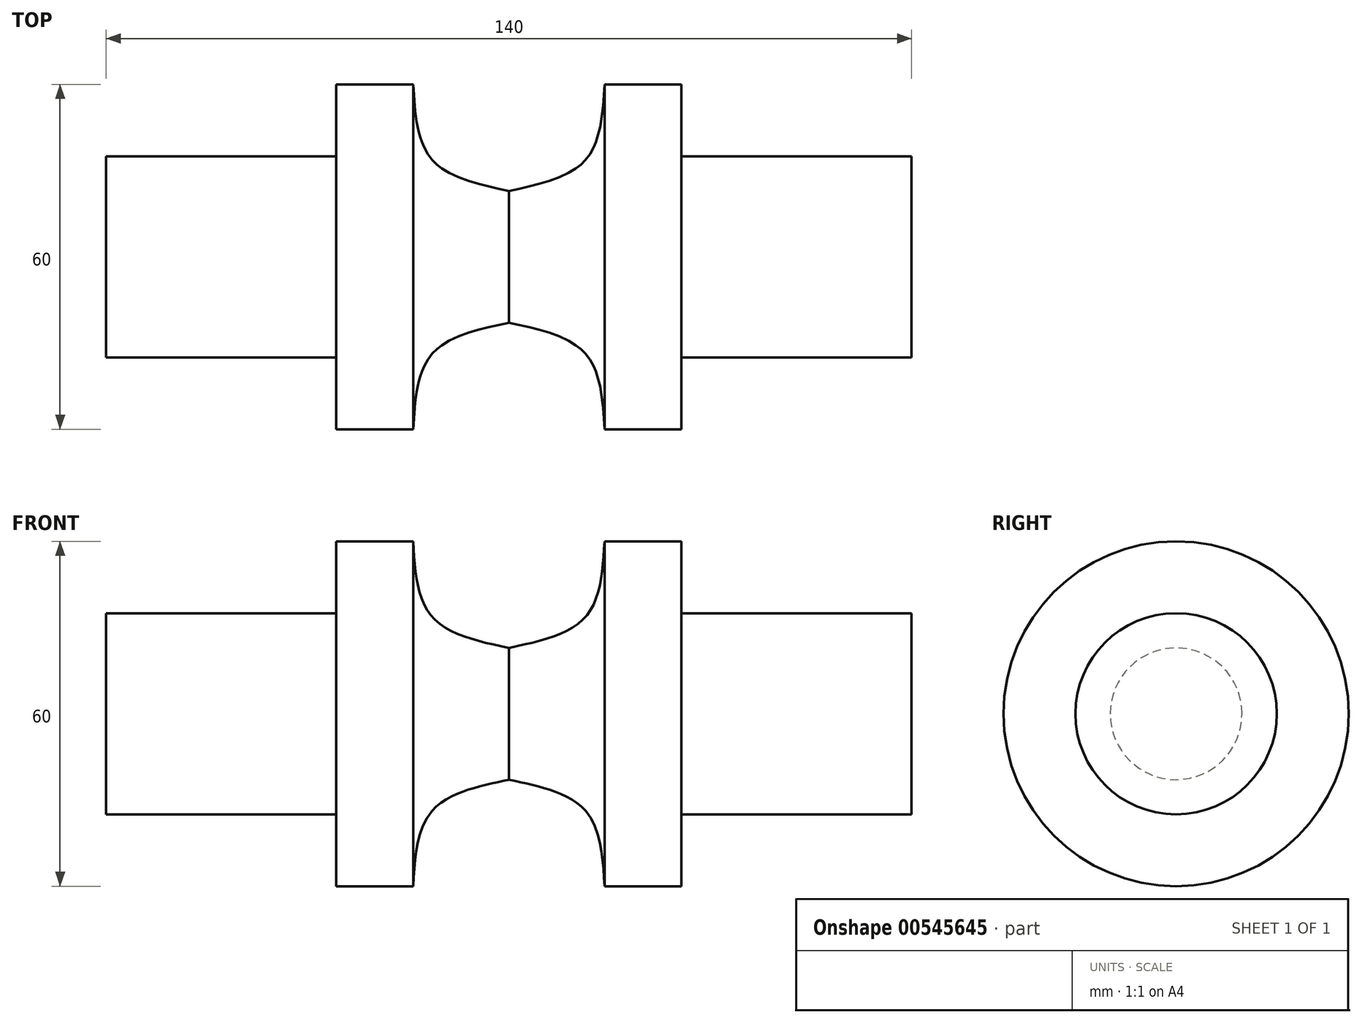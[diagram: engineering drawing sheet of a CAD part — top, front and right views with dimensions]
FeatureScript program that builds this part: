
annotation { "Feature Type Name" : "Feature", "Feature Type Description" : "" }
export const myFeature = defineFeature(function(context is Context, id is Id, definition is map)
    precondition{}
    {
        {
            var Q0;
            Q0=qCreatedBy(makeId("Front.planeOp"),FACE);
            var sketch = newSketch(context, id + "F0", { "sketchPlane" : qUnion([Q0])});
            skLineSegment(sketch, "E0", {"start": v(0, 0) * mm, "end": v(70, 0) * mm});
            skLineSegment(sketch, "E1", {"start": v(70, 0) * mm, "end": v(70, 17.5) * mm});
            skLineSegment(sketch, "E2", {"start": v(70, 17.5) * mm, "end": v(30, 17.5) * mm});
            skLineSegment(sketch, "E3", {"start": v(30, 17.5) * mm, "end": v(30, 30) * mm});
            skLineSegment(sketch, "E4", {"start": v(30, 30) * mm, "end": v(16.64, 30) * mm});
            skFitSpline(sketch, "E5", {"points": [v(16.64, 30) * mm, v(13.36, 16.9) * mm, v(0, 11.45) * mm], "startDerivative": vector(-1.83, -30.54) * mm, "endDerivative": vector(-31.27, -6.69) * mm});
            skLineSegment(sketch, "E6", {"start": v(0, 11.45) * mm, "end": v(0, 0) * mm});
            skSolve(sketch);
        }
        {
            var Q0;
            Q0 = qSketchRegion(id + "F0", true);
            var Q1;
            Q1=sQuery(id+"F0.wireOp",EDGE,"E0");
            revolve(context, id + "F1", {"entities" : qUnion([Q0]), "axis" : qUnion([Q1]), "revolveType" : RevolveType.FULL});
        }
        {
            var Q0;
            Q0=makeQuery(id+"F1.opRevolve","SWEPT_BODY",BODY,{"disambiguationData":[OSD([sQuery(id+"F0.wireOp",EDGE,"E0"),sQuery(id+"F0.wireOp",EDGE,"E1"),sQuery(id+"F0.wireOp",EDGE,"E2"),sQuery(id+"F0.wireOp",EDGE,"E3"),sQuery(id+"F0.wireOp",EDGE,"E4"),sQuery(id+"F0.wireOp",EDGE,"E5"),sQuery(id+"F0.wireOp",EDGE,"E6")])]});
            var Q1;
            Q1=makeQuery(id+"F1.opRevolve","SWEPT_FACE",FACE,{"disambiguationData":[OSD([sQuery(id+"F0.wireOp",EDGE,"E6")])]});
            mirror(context, id + "F2", {"operationType" : NewBodyOperationType.ADD, "entities" : qUnion([Q0]), "mirrorPlane" : qUnion([Q1])});
        }
    });
